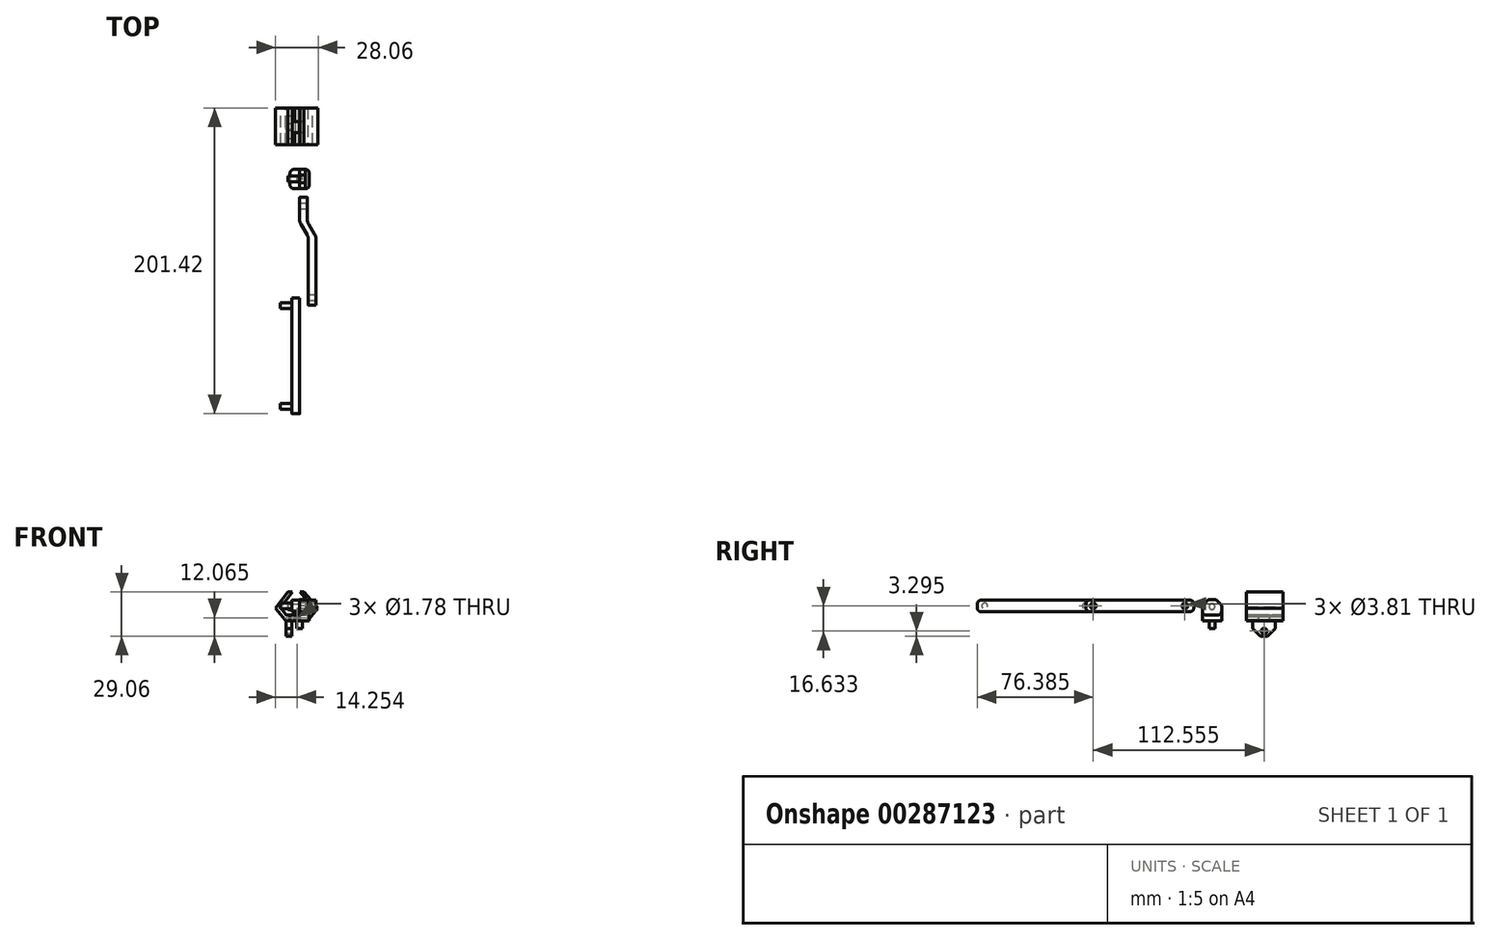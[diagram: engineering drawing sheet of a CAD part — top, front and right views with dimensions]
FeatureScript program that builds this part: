
annotation { "Feature Type Name" : "Feature", "Feature Type Description" : "" }
export const myFeature = defineFeature(function(context is Context, id is Id, definition is map)
    precondition{}
    {
        {
            var Q0;
            Q0=qCreatedBy(makeId("Top.planeOp"),FACE);
            var sketch = newSketch(context, id + "F0", { "sketchPlane" : qUnion([Q0])});
            skCircle(sketch, "E0", {"center": v(0, 0) * mm, "radius": 1.9 * mm});
            skLineSegment(sketch, "E1.bottom", {"start": v(-6.35, 6.35) * mm, "end": v(6.35, 6.35) * mm});
            skLineSegment(sketch, "E1.top", {"start": v(-6.35, -6.35) * mm, "end": v(6.35, -6.35) * mm});
            skLineSegment(sketch, "E1.left", {"start": v(-6.35, 6.35) * mm, "end": v(-6.35, -6.35) * mm});
            skLineSegment(sketch, "E1.right", {"start": v(6.35, 6.35) * mm, "end": v(6.35, -6.35) * mm});
            skSolve(sketch);
        }
        {
            var Q0;
            Q0=makeQuery(id+"F0.imprint","IMPRINT",FACE,{"disambiguationData":[TD([[makeQuery(id+"F0.imprint","IMPRINT",EDGE,{"derivedFrom":sQuery(id+"F0.wireOp",EDGE,"E0")}),1.0]])]});
            extrude(context, id + "F1", {"entities" : qUnion([Q0]), "oppositeDirection" : true, "depth" : 5.08 * mm});
        }
        {
            var Q0;
            Q0=makeQuery(id+"F0.imprint","IMPRINT",FACE,{"disambiguationData":[TD([[makeQuery(id+"F0.imprint","IMPRINT",EDGE,{"derivedFrom":sQuery(id+"F0.wireOp",EDGE,"E0")}),-1.0]])]});
            var Q1;
            Q1=makeQuery(id+"F0.imprint","IMPRINT",FACE,{"disambiguationData":[TD([[makeQuery(id+"F0.imprint","IMPRINT",EDGE,{"derivedFrom":sQuery(id+"F0.wireOp",EDGE,"E0")}),1.0]])]});
            extrude(context, id + "F2", {"entities" : qUnion([Q0, Q1]), "operationType" : NewBodyOperationType.ADD, "depth" : 3.8 * mm});
        }
        {
            var Q0;
            Q0=makeQuery(id+"F2.opExtrude","SWEPT_EDGE",EDGE,{"disambiguationData":[OSD([sQuery(id+"F0.wireOp",EDGE,"E1.bottom"),sQuery(id+"F0.wireOp",EDGE,"E1.left")])]});
            var Q1;
            Q1=makeQuery(id+"F2.opExtrude","SWEPT_EDGE",EDGE,{"disambiguationData":[OSD([sQuery(id+"F0.wireOp",EDGE,"E1.bottom"),sQuery(id+"F0.wireOp",EDGE,"E1.right")])]});
            var Q2;
            Q2=makeQuery(id+"F2.opExtrude","SWEPT_EDGE",EDGE,{"disambiguationData":[OSD([sQuery(id+"F0.wireOp",EDGE,"E1.top"),sQuery(id+"F0.wireOp",EDGE,"E1.left")])]});
            var Q3;
            Q3=makeQuery(id+"F2.opExtrude","SWEPT_EDGE",EDGE,{"disambiguationData":[OSD([sQuery(id+"F0.wireOp",EDGE,"E1.top"),sQuery(id+"F0.wireOp",EDGE,"E1.right")])]});
            fillet(context, id + "F3", {"entities" : qUnion([Q0, Q1, Q2, Q3]), "radius" : 2.54 * mm, "tangentPropagation" : true, "allowEdgeOverflow" : false});
        }
        {
            var Q0;
            Q0=makeQuery(id+"F2.opExtrude","CAP_FACE",FACE,{"disambiguationData":[OSD([sQuery(id+"F0.wireOp",EDGE,"E1.bottom"),sQuery(id+"F0.wireOp",EDGE,"E1.top"),sQuery(id+"F0.wireOp",EDGE,"E1.left"),sQuery(id+"F0.wireOp",EDGE,"E1.right")])],"isStart":false});
            var sketch = newSketch(context, id + "F4", { "sketchPlane" : qUnion([Q0])});
            skLineSegment(sketch, "E2.bottom", {"start": v(0, 6.35) * mm, "end": v(3.8, 6.35) * mm});
            skLineSegment(sketch, "E2.top", {"start": v(0, -6.35) * mm, "end": v(3.8, -6.35) * mm});
            skLineSegment(sketch, "E2.left", {"start": v(0, 6.35) * mm, "end": v(0, -6.35) * mm});
            skLineSegment(sketch, "E2.right", {"start": v(3.8, 6.35) * mm, "end": v(3.8, -6.35) * mm});
            skSolve(sketch);
        }
        {
            var Q0;
            Q0=makeQuery(id+"F4.imprint","IMPRINT",FACE,{"disambiguationData":[TD([[makeQuery(id+"F4.imprint","IMPRINT",EDGE,{"derivedFrom":sQuery(id+"F4.wireOp",EDGE,"E2.bottom")}),-1.0]])]});
            extrude(context, id + "F5", {"entities" : qUnion([Q0]), "operationType" : NewBodyOperationType.ADD, "depth" : 10.16 * mm});
        }
        {
            var Q0;
            Q0=makeQuery(id+"F5.opExtrude","CAP_EDGE",EDGE,{"disambiguationData":[OSD([sQuery(id+"F4.wireOp",EDGE,"E2.top")])],"isStart":false});
            var Q1;
            Q1=makeQuery(id+"F5.opExtrude","CAP_EDGE",EDGE,{"disambiguationData":[OSD([sQuery(id+"F4.wireOp",EDGE,"E2.bottom")])],"isStart":false});
            chamfer(context, id + "F6", {"entities" : qUnion([Q0, Q1]), "width" : 3.8 * mm, "tangentPropagation" : true});
        }
        {
            var Q0;
            Q0=makeQuery(id+"F5.opExtrude","SWEPT_FACE",FACE,{"disambiguationData":[OSD([sQuery(id+"F4.wireOp",EDGE,"E2.left")])]});
            var sketch = newSketch(context, id + "F7", { "sketchPlane" : qUnion([Q0])});
            skCircle(sketch, "E3", {"center": v(0, 9.29) * mm, "radius": 1.9 * mm});
            skPoint(sketch, "E3.centerSnap0", {"position": v(0, 13.97) * mm});
            skSolve(sketch);
        }
        {
            var Q0;
            Q0=makeQuery(id+"F7.imprint","IMPRINT",FACE,{"disambiguationData":[TD([[makeQuery(id+"F7.imprint","IMPRINT",EDGE,{"derivedFrom":sQuery(id+"F7.wireOp",EDGE,"E3")}),1.0]])]});
            extrude(context, id + "F8", {"entities" : qUnion([Q0]), "operationType" : NewBodyOperationType.ADD, "depth" : 7.62 * mm});
        }
        {
            var Q0;
            Q0=makeQuery(id+"F5.opExtrude","CAP_EDGE",EDGE,{"disambiguationData":[OSD([sQuery(id+"F4.wireOp",EDGE,"E2.right")])],"isStart":true});
            fillet(context, id + "F9", {"entities" : qUnion([Q0]), "radius" : 5.08 * mm, "tangentPropagation" : true, "allowEdgeOverflow" : false});
        }
        {
            var Q0;
            Q0=qCreatedBy(makeId("Right.planeOp"),FACE);
            var sketch = newSketch(context, id + "F10", { "sketchPlane" : qUnion([Q0])});
            skCircle(sketch, "E4", {"center": v(-17.87, 9.77) * mm, "radius": 1.9 * mm});
            skLineSegment(sketch, "E5.bottom", {"start": v(-23.78, 13.58) * mm, "end": v(-11.96, 13.58) * mm});
            skLineSegment(sketch, "E5.top", {"start": v(-23.78, 5.96) * mm, "end": v(-11.96, 5.96) * mm});
            skLineSegment(sketch, "E5.right", {"start": v(-11.96, 13.58) * mm, "end": v(-11.96, 5.96) * mm});
            skLineSegment(sketch, "E6.bottom", {"start": v(-23.78, 13.58) * mm, "end": v(-28.47, 13.58) * mm});
            skLineSegment(sketch, "E6.top", {"start": v(-23.78, 5.96) * mm, "end": v(-28.47, 5.96) * mm});
            skLineSegment(sketch, "E6.right", {"start": v(-28.47, 13.58) * mm, "end": v(-28.47, 5.96) * mm});
            skSolve(sketch);
        }
        {
            var Q0;
            Q0=makeQuery(id+"F10.imprint","IMPRINT",FACE,{"disambiguationData":[TD([[makeQuery(id+"F10.imprint","IMPRINT",EDGE,{"derivedFrom":sQuery(id+"F10.wireOp",EDGE,"E4")}),-1.0]])]});
            extrude(context, id + "F11", {"entities" : qUnion([Q0]), "depth" : 5.08 * mm});
        }
        {
            var Q0;
            Q0=makeQuery(id+"F11.opExtrude","SWEPT_FACE",FACE,{"disambiguationData":[OSD([sQuery(id+"F10.wireOp",EDGE,"E5.bottom"),sQuery(id+"F10.wireOp",EDGE,"E6.bottom")])]});
            var sketch = newSketch(context, id + "F12", { "sketchPlane" : qUnion([Q0])});
            skLineSegment(sketch, "E7", {"start": v(5.08, -28.47) * mm, "end": v(10.64, -37.52) * mm});
            skLineSegment(sketch, "E8", {"start": v(10.64, -37.52) * mm, "end": v(10.64, -83.05) * mm});
            skLineSegment(sketch, "E9", {"start": v(10.64, -83.05) * mm, "end": v(5.56, -83.05) * mm});
            skLineSegment(sketch, "E10", {"start": v(5.56, -83.05) * mm, "end": v(5.56, -37.77) * mm});
            skLineSegment(sketch, "E11", {"start": v(5.56, -37.77) * mm, "end": v(0, -28.47) * mm});
            skSolve(sketch);
        }
        {
            var Q0;
            Q0=makeQuery(id+"F12.imprint","IMPRINT",FACE,{"disambiguationData":[TD([[makeQuery(id+"F12.imprint","IMPRINT",EDGE,{"derivedFrom":sQuery(id+"F12.wireOp",EDGE,"E7")}),-1.0]])]});
            extrude(context, id + "F13", {"entities" : qUnion([Q0]), "operationType" : NewBodyOperationType.ADD, "oppositeDirection" : true, "depth" : 7.62 * mm});
        }
        {
            var Q0;
            Q0=makeQuery(id+"F13.opExtrude","SWEPT_FACE",FACE,{"disambiguationData":[OSD([sQuery(id+"F12.wireOp",EDGE,"E10")])]});
            var sketch = newSketch(context, id + "F14", { "sketchPlane" : qUnion([Q0])});
            skCircle(sketch, "E12", {"center": v(78.21, 9.77) * mm, "radius": 1.9 * mm});
            skPoint(sketch, "E12.centerSnap0", {"position": v(83.05, 9.77) * mm});
            skSolve(sketch);
        }
        {
            var Q0;
            Q0=makeQuery(id+"F14.imprint","IMPRINT",FACE,{"disambiguationData":[TD([[makeQuery(id+"F14.imprint","IMPRINT",EDGE,{"derivedFrom":sQuery(id+"F14.wireOp",EDGE,"E12")}),1.0]])]});
            extrude(context, id + "F15", {"entities" : qUnion([Q0]), "operationType" : NewBodyOperationType.REMOVE, "oppositeDirection" : true, "depth" : 25.4 * mm});
        }
        {
            var Q0;
            Q0=makeQuery(id+"F11.opExtrude","SWEPT_EDGE",EDGE,{"disambiguationData":[OSD([sQuery(id+"F10.wireOp",EDGE,"E5.bottom"),sQuery(id+"F10.wireOp",EDGE,"E5.right")])]});
            var Q1;
            Q1=makeQuery(id+"F13.opExtrude","CAP_EDGE",EDGE,{"disambiguationData":[OSD([sQuery(id+"F12.wireOp",EDGE,"E9")])],"isStart":true});
            var Q2;
            Q2=makeQuery(id+"F13.opExtrude","CAP_EDGE",EDGE,{"disambiguationData":[OSD([sQuery(id+"F12.wireOp",EDGE,"E9")])],"isStart":false});
            var Q3;
            Q3=makeQuery(id+"F11.opExtrude","SWEPT_EDGE",EDGE,{"disambiguationData":[OSD([sQuery(id+"F10.wireOp",EDGE,"E5.top"),sQuery(id+"F10.wireOp",EDGE,"E5.right")])]});
            fillet(context, id + "F16", {"entities" : qUnion([Q0, Q1, Q2, Q3]), "radius" : 2.54 * mm, "tangentPropagation" : true, "allowEdgeOverflow" : false});
        }
        {
            var Q0;
            {var subQ0=sQuery(id+"F10.wireOp",EDGE,"E6.right");Q0=makeQuery(id+"F13.boolean.opBoolean","MERGE",EDGE,{"derivedFrom":[makeQuery(id+"F11.opExtrude","CAP_EDGE",EDGE,{"disambiguationData":[OSD([subQ0])],"isStart":false}),makeQuery(id+"F13.opExtrude","SWEPT_EDGE",EDGE,{"disambiguationData":[OSD([sQuery(id+"F10.wireOp",EDGE,"E5.bottom"),sQuery(id+"F10.wireOp",EDGE,"E6.bottom"),subQ0,sQuery(id+"F12.wireOp",EDGE,"E7")])]})]});}
            var Q1;
            Q1=makeQuery(id+"F13.opExtrude","SWEPT_EDGE",EDGE,{"disambiguationData":[OSD([sQuery(id+"F12.wireOp",EDGE,"E7"),sQuery(id+"F12.wireOp",EDGE,"E8")])]});
            var Q2;
            {var subQ0=sQuery(id+"F10.wireOp",EDGE,"E6.right");Q2=makeQuery(id+"F13.boolean.opBoolean","MERGE",EDGE,{"derivedFrom":[makeQuery(id+"F11.opExtrude","CAP_EDGE",EDGE,{"disambiguationData":[OSD([subQ0])],"isStart":true}),makeQuery(id+"F13.opExtrude","SWEPT_EDGE",EDGE,{"disambiguationData":[OSD([sQuery(id+"F10.wireOp",EDGE,"E5.bottom"),sQuery(id+"F10.wireOp",EDGE,"E6.bottom"),subQ0,sQuery(id+"F12.wireOp",EDGE,"E11")])]})]});}
            var Q3;
            Q3=makeQuery(id+"F13.opExtrude","SWEPT_EDGE",EDGE,{"disambiguationData":[OSD([sQuery(id+"F12.wireOp",EDGE,"E10"),sQuery(id+"F12.wireOp",EDGE,"E11")])]});
            fillet(context, id + "F17", {"entities" : qUnion([Q0, Q1, Q2, Q3]), "radius" : 5.08 * mm, "tangentPropagation" : true, "allowEdgeOverflow" : false});
        }
        {
            var Q0;
            Q0=qCreatedBy(makeId("Right.planeOp"),FACE);
            var sketch = newSketch(context, id + "F18", { "sketchPlane" : qUnion([Q0])});
            skLineSegment(sketch, "E13.bottom", {"start": v(-78.4, 13.54) * mm, "end": v(-154.6, 13.54) * mm});
            skLineSegment(sketch, "E13.top", {"start": v(-78.4, 5.92) * mm, "end": v(-154.6, 5.92) * mm});
            skLineSegment(sketch, "E13.left", {"start": v(-78.4, 13.54) * mm, "end": v(-78.4, 5.92) * mm});
            skLineSegment(sketch, "E13.right", {"start": v(-154.6, 13.54) * mm, "end": v(-154.6, 5.92) * mm});
            skCircle(sketch, "E14", {"center": v(-149.65, 9.73) * mm, "radius": 1.9 * mm});
            skPoint(sketch, "E14.centerSnap0", {"position": v(-154.6, 9.73) * mm});
            skCircle(sketch, "E15", {"center": v(-83.4, 9.73) * mm, "radius": 1.9 * mm});
            skPoint(sketch, "E15.centerSnap0", {"position": v(-78.4, 9.73) * mm});
            skSolve(sketch);
        }
        {
            var Q0;
            Q0=makeQuery(id+"F18.imprint","IMPRINT",FACE,{"disambiguationData":[TD([[makeQuery(id+"F18.imprint","IMPRINT",EDGE,{"derivedFrom":sQuery(id+"F18.wireOp",EDGE,"E13.bottom")}),1.0]])]});
            extrude(context, id + "F19", {"entities" : qUnion([Q0]), "oppositeDirection" : true, "depth" : 5.08 * mm});
        }
        {
            var Q0;
            Q0=makeQuery(id+"F18.imprint","IMPRINT",FACE,{"disambiguationData":[TD([[makeQuery(id+"F18.imprint","IMPRINT",EDGE,{"derivedFrom":sQuery(id+"F18.wireOp",EDGE,"E15")}),1.0]])]});
            var Q1;
            Q1=makeQuery(id+"F18.imprint","IMPRINT",FACE,{"disambiguationData":[TD([[makeQuery(id+"F18.imprint","IMPRINT",EDGE,{"derivedFrom":sQuery(id+"F18.wireOp",EDGE,"E14")}),1.0]])]});
            extrude(context, id + "F20", {"entities" : qUnion([Q0, Q1]), "operationType" : NewBodyOperationType.ADD, "oppositeDirection" : true, "depth" : 12.7 * mm});
        }
        {
            var Q0;
            Q0=makeQuery(id+"F19.opExtrude","SWEPT_EDGE",EDGE,{"disambiguationData":[OSD([sQuery(id+"F18.wireOp",EDGE,"E13.bottom"),sQuery(id+"F18.wireOp",EDGE,"E13.right")])]});
            var Q1;
            Q1=makeQuery(id+"F19.opExtrude","SWEPT_EDGE",EDGE,{"disambiguationData":[OSD([sQuery(id+"F18.wireOp",EDGE,"E13.top"),sQuery(id+"F18.wireOp",EDGE,"E13.right")])]});
            var Q2;
            Q2=makeQuery(id+"F19.opExtrude","SWEPT_EDGE",EDGE,{"disambiguationData":[OSD([sQuery(id+"F18.wireOp",EDGE,"E13.bottom"),sQuery(id+"F18.wireOp",EDGE,"E13.left")])]});
            var Q3;
            Q3=makeQuery(id+"F19.opExtrude","SWEPT_EDGE",EDGE,{"disambiguationData":[OSD([sQuery(id+"F18.wireOp",EDGE,"E13.top"),sQuery(id+"F18.wireOp",EDGE,"E13.left")])]});
            fillet(context, id + "F21", {"entities" : qUnion([Q0, Q1, Q2, Q3]), "radius" : 2.54 * mm, "tangentPropagation" : true, "allowEdgeOverflow" : false});
        }
        {
            var Q0;
            Q0=qCreatedBy(makeId("Top.planeOp"),FACE);
            var sketch = newSketch(context, id + "F22", { "sketchPlane" : qUnion([Q0])});
            skLineSegment(sketch, "E16.bottom", {"start": v(-15.5, 47.75) * mm, "end": v(15.5, 47.75) * mm, "construction": true});
            skLineSegment(sketch, "E16.top", {"start": v(-15.5, 20.63) * mm, "end": v(15.5, 20.63) * mm, "construction": true});
            skLineSegment(sketch, "E16.left", {"start": v(-15.5, 47.75) * mm, "end": v(-15.5, 20.63) * mm, "construction": true});
            skLineSegment(sketch, "E16.right", {"start": v(15.5, 47.75) * mm, "end": v(15.5, 20.63) * mm, "construction": true});
            skPoint(sketch, "E16.middle", {"position": v(0, 34.2) * mm});
            skLineSegment(sketch, "E17", {"start": v(0, 37.83) * mm, "end": v(0, 30.63) * mm});
            skLineSegment(sketch, "E18", {"start": v(0, 30.63) * mm, "end": v(-3.32, 30.63) * mm});
            skLineSegment(sketch, "E19", {"start": v(-3.32, 30.63) * mm, "end": v(-3.32, 22.66) * mm});
            skLineSegment(sketch, "E20", {"start": v(-3.32, 22.66) * mm, "end": v(-9.16, 22.66) * mm});
            skLineSegment(sketch, "E21", {"start": v(-9.16, 22.66) * mm, "end": v(-9.16, 46.82) * mm});
            skLineSegment(sketch, "E22", {"start": v(-9.16, 46.82) * mm, "end": v(-3.32, 46.82) * mm});
            skLineSegment(sketch, "E23", {"start": v(-3.32, 46.82) * mm, "end": v(-3.32, 37.83) * mm});
            skLineSegment(sketch, "E24", {"start": v(-3.32, 37.83) * mm, "end": v(0, 37.83) * mm});
            skLineSegment(sketch, "E25.0", {"start": v(-3.2, 30.5) * mm, "end": v(-3.2, 22.66) * mm});
            skLineSegment(sketch, "E25.1", {"start": v(-3.2, 46.82) * mm, "end": v(-3.2, 37.95) * mm});
            skLineSegment(sketch, "E25.2", {"start": v(-3.2, 37.95) * mm, "end": v(0.13, 37.95) * mm});
            skLineSegment(sketch, "E25.3", {"start": v(0.13, 37.95) * mm, "end": v(0.13, 30.5) * mm});
            skLineSegment(sketch, "E25.4", {"start": v(0.13, 30.5) * mm, "end": v(-3.2, 30.5) * mm});
            skLineSegment(sketch, "E26", {"start": v(-3.2, 46.82) * mm, "end": v(5.2, 46.82) * mm});
            skLineSegment(sketch, "E27", {"start": v(5.2, 46.82) * mm, "end": v(5.2, 22.66) * mm});
            skLineSegment(sketch, "E28", {"start": v(5.2, 22.66) * mm, "end": v(-3.2, 22.66) * mm});
            skLineSegment(sketch, "E29", {"start": v(-1.66, 46.82) * mm, "end": v(-1.66, 22.66) * mm, "construction": true});
            skPoint(sketch, "E29.startSnap0", {"position": v(-1.66, 37.83) * mm});
            skSolve(sketch);
        }
        {
            var Q0;
            Q0=makeQuery(id+"F22.imprint","IMPRINT",FACE,{"disambiguationData":[TD([[makeQuery(id+"F22.imprint","IMPRINT",EDGE,{"derivedFrom":sQuery(id+"F22.wireOp",EDGE,"E25.0")}),1.0]])]});
            var Q1;
            Q1=makeQuery(id+"F22.imprint","IMPRINT",FACE,{"disambiguationData":[TD([[makeQuery(id+"F22.imprint","IMPRINT",EDGE,{"derivedFrom":sQuery(id+"F22.wireOp",EDGE,"E17")}),-1.0]])]});
            extrude(context, id + "F23", {"entities" : qUnion([Q0, Q1]), "depth" : 3.8 * mm});
        }
        {
            var Q0;
            Q0=makeQuery(id+"F23.opExtrude","SWEPT_FACE",FACE,{"disambiguationData":[OSD([sQuery(id+"F22.wireOp",EDGE,"E26")])]});
            var sketch = newSketch(context, id + "F24", { "sketchPlane" : qUnion([Q0])});
            skCircle(sketch, "E30", {"center": v(1.66, 1.9) * mm, "radius": 0.89 * mm});
            skPoint(sketch, "E30.centerSnap0", {"position": v(3.2, 1.9) * mm});
            skSolve(sketch);
        }
        {
            var Q0;
            Q0=makeQuery(id+"F24.imprint","IMPRINT",FACE,{"disambiguationData":[TD([[makeQuery(id+"F24.imprint","IMPRINT",EDGE,{"derivedFrom":sQuery(id+"F24.wireOp",EDGE,"E30")}),1.0]])]});
            extrude(context, id + "F25", {"entities" : qUnion([Q0]), "operationType" : NewBodyOperationType.REMOVE, "oppositeDirection" : true, "depth" : 27.3 * mm});
        }
        {
            var Q0;
            Q0=makeQuery(id+"F23.opExtrude","CAP_EDGE",EDGE,{"disambiguationData":[OSD([sQuery(id+"F22.wireOp",EDGE,"E23")])],"isStart":false});
            var Q1;
            Q1=makeQuery(id+"F23.opExtrude","CAP_EDGE",EDGE,{"disambiguationData":[OSD([sQuery(id+"F22.wireOp",EDGE,"E23")])],"isStart":true});
            var Q2;
            Q2=makeQuery(id+"F23.opExtrude","CAP_EDGE",EDGE,{"disambiguationData":[OSD([sQuery(id+"F22.wireOp",EDGE,"E25.1")])],"isStart":false});
            var Q3;
            Q3=makeQuery(id+"F23.opExtrude","CAP_EDGE",EDGE,{"disambiguationData":[OSD([sQuery(id+"F22.wireOp",EDGE,"E25.1")])],"isStart":true});
            var Q4;
            Q4=makeQuery(id+"F23.opExtrude","CAP_EDGE",EDGE,{"disambiguationData":[OSD([sQuery(id+"F22.wireOp",EDGE,"E19")])],"isStart":false});
            var Q5;
            Q5=makeQuery(id+"F23.opExtrude","CAP_EDGE",EDGE,{"disambiguationData":[OSD([sQuery(id+"F22.wireOp",EDGE,"E25.0")])],"isStart":false});
            var Q6;
            Q6=makeQuery(id+"F23.opExtrude","CAP_EDGE",EDGE,{"disambiguationData":[OSD([sQuery(id+"F22.wireOp",EDGE,"E17")])],"isStart":false});
            var Q7;
            Q7=makeQuery(id+"F23.opExtrude","CAP_EDGE",EDGE,{"disambiguationData":[OSD([sQuery(id+"F22.wireOp",EDGE,"E25.3")])],"isStart":false});
            var Q8;
            Q8=makeQuery(id+"F23.opExtrude","CAP_EDGE",EDGE,{"disambiguationData":[OSD([sQuery(id+"F22.wireOp",EDGE,"E17")])],"isStart":true});
            var Q9;
            Q9=makeQuery(id+"F23.opExtrude","CAP_EDGE",EDGE,{"disambiguationData":[OSD([sQuery(id+"F22.wireOp",EDGE,"E25.3")])],"isStart":true});
            var Q10;
            Q10=makeQuery(id+"F23.opExtrude","CAP_EDGE",EDGE,{"disambiguationData":[OSD([sQuery(id+"F22.wireOp",EDGE,"E25.0")])],"isStart":true});
            var Q11;
            Q11=makeQuery(id+"F23.opExtrude","CAP_EDGE",EDGE,{"disambiguationData":[OSD([sQuery(id+"F22.wireOp",EDGE,"E19")])],"isStart":true});
            fillet(context, id + "F26", {"entities" : qUnion([Q0, Q1, Q2, Q3, Q4, Q5, Q6, Q7, Q8, Q9, Q10, Q11]), "radius" : 1.78 * mm, "tangentPropagation" : true, "allowEdgeOverflow" : false});
        }
        {
            var Q0;
            Q0=makeQuery(id+"F23.opExtrude","SWEPT_FACE",FACE,{"disambiguationData":[OSD([sQuery(id+"F22.wireOp",EDGE,"E26")])]});
            var sketch = newSketch(context, id + "F27", { "sketchPlane" : qUnion([Q0])});
            skLineSegment(sketch, "E31", {"start": v(-5.2, 3.8) * mm, "end": v(-8.47, 9.07) * mm});
            skLineSegment(sketch, "E32", {"start": v(-8.47, 9.07) * mm, "end": v(-0.38, 18.9) * mm});
            skLineSegment(sketch, "E33", {"start": v(-0.38, 18.9) * mm, "end": v(-2.84, 18.9) * mm});
            skLineSegment(sketch, "E34", {"start": v(-2.84, 18.9) * mm, "end": v(-12.15, 8.28) * mm});
            skLineSegment(sketch, "E35", {"start": v(-12.15, 8.28) * mm, "end": v(-5.2, 0) * mm});
            skLineSegment(sketch, "E36", {"start": v(9.1, 3.81) * mm, "end": v(12.4, 8.59) * mm});
            skLineSegment(sketch, "E37", {"start": v(12.4, 8.59) * mm, "end": v(4.75, 18.87) * mm});
            skLineSegment(sketch, "E38", {"start": v(4.75, 18.87) * mm, "end": v(7.87, 18.87) * mm});
            skLineSegment(sketch, "E39", {"start": v(7.87, 18.87) * mm, "end": v(15.91, 8.35) * mm});
            skLineSegment(sketch, "E40", {"start": v(15.91, 8.35) * mm, "end": v(9.04, 0) * mm});
            skLineSegment(sketch, "E41", {"start": v(9.04, 0) * mm, "end": v(9.1, 3.81) * mm});
            skSolve(sketch);
        }
        {
            var Q0;
            Q0=makeQuery(id+"F27.imprint","IMPRINT",FACE,{"disambiguationData":[TD([[makeQuery(id+"F27.imprint","IMPRINT",EDGE,{"derivedFrom":sQuery(id+"F27.wireOp",EDGE,"E31")}),1.0]])]});
            var Q1;
            Q1=makeQuery(id+"F27.imprint","IMPRINT",FACE,{"disambiguationData":[TD([[makeQuery(id+"F27.imprint","IMPRINT",EDGE,{"derivedFrom":sQuery(id+"F27.wireOp",EDGE,"E36")}),-1.0]])]});
            extrude(context, id + "F28", {"entities" : qUnion([Q0, Q1]), "oppositeDirection" : true, "depth" : 24.16 * mm});
        }
        {
            var Q0;
            Q0=makeQuery(id+"F22.imprint","IMPRINT",FACE,{"disambiguationData":[TD([[makeQuery(id+"F22.imprint","IMPRINT",EDGE,{"derivedFrom":sQuery(id+"F22.wireOp",EDGE,"E17")}),-1.0]])]});
            var sketch = newSketch(context, id + "F29", { "sketchPlane" : qUnion([Q0])});
            skLineSegment(sketch, "E42.bottom", {"start": v(-9.08, 41.82) * mm, "end": v(-5.15, 41.82) * mm});
            skLineSegment(sketch, "E42.top", {"start": v(-9.08, 26.86) * mm, "end": v(-5.15, 26.86) * mm});
            skLineSegment(sketch, "E42.left", {"start": v(-9.08, 41.82) * mm, "end": v(-9.08, 26.86) * mm});
            skLineSegment(sketch, "E42.right", {"start": v(-5.15, 41.82) * mm, "end": v(-5.15, 26.86) * mm});
            skPoint(sketch, "E42.middle", {"position": v(-7.11, 34.34) * mm});
            skSolve(sketch);
        }
        {
            var Q0;
            Q0=makeQuery(id+"F29.imprint","IMPRINT",FACE,{"disambiguationData":[TD([[makeQuery(id+"F29.imprint","IMPRINT",EDGE,{"derivedFrom":sQuery(id+"F29.wireOp",EDGE,"E42.bottom")}),-1.0]])]});
            extrude(context, id + "F30", {"entities" : qUnion([Q0]), "operationType" : NewBodyOperationType.ADD, "oppositeDirection" : true, "depth" : 10.16 * mm});
        }
        {
            var Q0;
            Q0=makeQuery(id+"F30.opExtrude","SWEPT_FACE",FACE,{"disambiguationData":[OSD([sQuery(id+"F29.wireOp",EDGE,"E42.left")])]});
            var sketch = newSketch(context, id + "F31", { "sketchPlane" : qUnion([Q0])});
            skCircle(sketch, "E43", {"center": v(-34.34, -6.86) * mm, "radius": 1.9 * mm});
            skPoint(sketch, "E43.centerSnap0", {"position": v(-34.34, -10.16) * mm});
            skSolve(sketch);
        }
        {
            var Q0;
            Q0=makeQuery(id+"F31.imprint","IMPRINT",FACE,{"disambiguationData":[TD([[makeQuery(id+"F31.imprint","IMPRINT",EDGE,{"derivedFrom":sQuery(id+"F31.wireOp",EDGE,"E43")}),1.0]])]});
            extrude(context, id + "F32", {"entities" : qUnion([Q0]), "operationType" : NewBodyOperationType.REMOVE, "oppositeDirection" : true, "depth" : 25.4 * mm});
        }
        {
            var Q0;
            Q0=makeQuery(id+"F30.opExtrude","CAP_EDGE",EDGE,{"disambiguationData":[OSD([sQuery(id+"F29.wireOp",EDGE,"E42.top")])],"isStart":false});
            var Q1;
            Q1=makeQuery(id+"F30.opExtrude","CAP_EDGE",EDGE,{"disambiguationData":[OSD([sQuery(id+"F29.wireOp",EDGE,"E42.bottom")])],"isStart":false});
            chamfer(context, id + "F33", {"entities" : qUnion([Q0, Q1]), "width" : 5.08 * mm, "tangentPropagation" : true});
        }
    });
